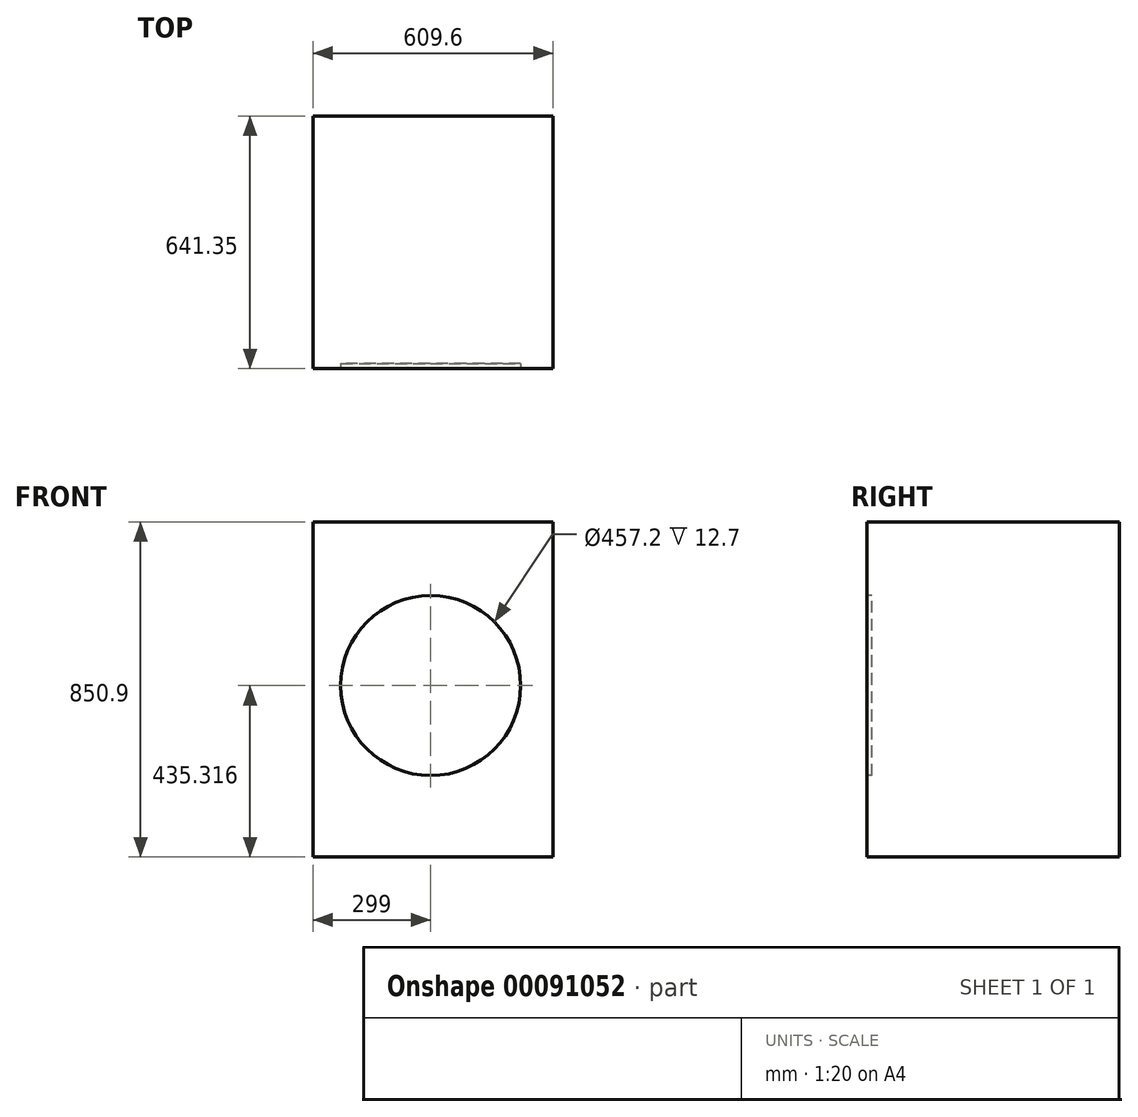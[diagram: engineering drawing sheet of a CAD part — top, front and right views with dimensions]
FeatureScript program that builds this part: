
annotation { "Feature Type Name" : "Feature", "Feature Type Description" : "" }
export const myFeature = defineFeature(function(context is Context, id is Id, definition is map)
    precondition{}
    {
        {
            var Q0;
            Q0=qCreatedBy(makeId("Top.planeOp"),FACE);
            var sketch = newSketch(context, id + "F0", { "sketchPlane" : qUnion([Q0])});
            skLineSegment(sketch, "E0.bottom", {"start": v(-299, 383.37) * mm, "end": v(310.6, 383.37) * mm});
            skLineSegment(sketch, "E0.top", {"start": v(-299, -257.98) * mm, "end": v(310.6, -257.98) * mm});
            skLineSegment(sketch, "E0.left", {"start": v(-299, 383.37) * mm, "end": v(-299, -257.98) * mm});
            skLineSegment(sketch, "E0.right", {"start": v(310.6, 383.37) * mm, "end": v(310.6, -257.98) * mm});
            skSolve(sketch);
        }
        {
            var Q0;
            Q0 = qSketchRegion(id + "F0", true);
            extrude(context, id + "F1", {"entities" : qUnion([Q0]), "depth" : 850.9 * mm});
        }
        {
            var Q0;
            Q0=makeQuery(id+"F1.opExtrude","SWEPT_FACE",FACE,{"disambiguationData":[OSD([sQuery(id+"F0.wireOp",EDGE,"E0.top")])]});
            var sketch = newSketch(context, id + "F2", { "sketchPlane" : qUnion([Q0])});
            skCircle(sketch, "E1", {"center": v(0, 435.32) * mm, "radius": 228.6 * mm});
            skSolve(sketch);
        }
        {
            var Q0;
            Q0 = qSketchRegion(id + "F2", true);
            extrude(context, id + "F3", {"entities" : qUnion([Q0]), "operationType" : NewBodyOperationType.REMOVE, "oppositeDirection" : true, "depth" : 12.7 * mm});
        }
    });
